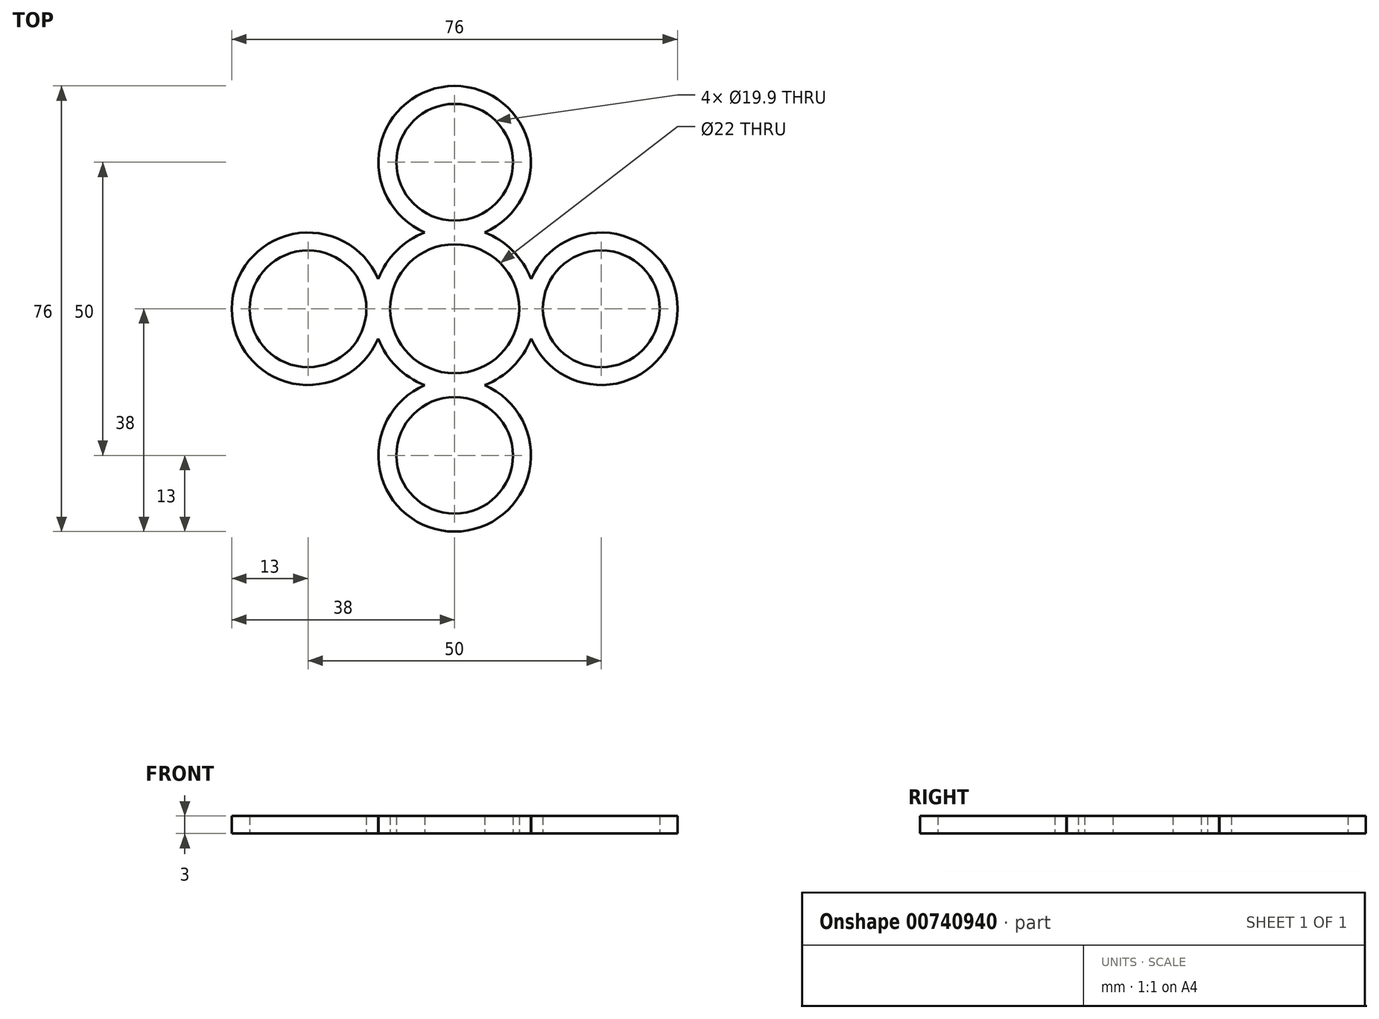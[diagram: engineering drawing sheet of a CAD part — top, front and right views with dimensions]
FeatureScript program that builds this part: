
annotation { "Feature Type Name" : "Feature", "Feature Type Description" : "" }
export const myFeature = defineFeature(function(context is Context, id is Id, definition is map)
    precondition{}
    {
        {
            var Q0;
            Q0=qCreatedBy(makeId("Top.planeOp"),FACE);
            var sketch = newSketch(context, id + "F0", { "sketchPlane" : qUnion([Q0])});
            skArc(sketch, "E0", {"start": v(7.78, 7.78) * mm, "mid": v(0, 11) * mm, "end": v(-7.78, 7.78) * mm});
            skCircle(sketch, "E1", {"center": v(0, 25) * mm, "radius": 9.95 * mm});
            skArc(sketch, "E2", {"start": v(-5.1, 13.04) * mm, "mid": v(-7.66, 11.72) * mm, "end": v(-9.9, 9.9) * mm});
            skArc(sketch, "E3", {"start": v(5.1, 13.04) * mm, "mid": v(0, 38) * mm, "end": v(-5.1, 13.04) * mm});
            skArc(sketch, "E4.trimOffspring", {"start": v(9.9, 9.9) * mm, "mid": v(7.66, 11.72) * mm, "end": v(5.1, 13.04) * mm});
            skArc(sketch, "E5.1.0", {"start": v(-13.04, 5.1) * mm, "mid": v(-38, 0) * mm, "end": v(-13.04, -5.1) * mm});
            skCircle(sketch, "E5.1.1", {"center": v(-25, 0) * mm, "radius": 9.95 * mm});
            skArc(sketch, "E5.1.2", {"start": v(-7.78, 7.78) * mm, "mid": v(-11, 0) * mm, "end": v(-7.78, -7.78) * mm});
            skArc(sketch, "E5.1.3", {"start": v(-13.04, -5.1) * mm, "mid": v(-11.72, -7.66) * mm, "end": v(-9.9, -9.9) * mm});
            skArc(sketch, "E5.1.4", {"start": v(-9.9, 9.9) * mm, "mid": v(-11.72, 7.66) * mm, "end": v(-13.04, 5.1) * mm});
            skArc(sketch, "E5.2.0", {"start": v(-5.1, -13.04) * mm, "mid": v(0, -38) * mm, "end": v(5.1, -13.04) * mm});
            skCircle(sketch, "E5.2.1", {"center": v(0, -25) * mm, "radius": 9.95 * mm});
            skArc(sketch, "E5.2.2", {"start": v(-7.78, -7.78) * mm, "mid": v(0, -11) * mm, "end": v(7.78, -7.78) * mm});
            skArc(sketch, "E5.2.3", {"start": v(5.1, -13.04) * mm, "mid": v(7.66, -11.72) * mm, "end": v(9.9, -9.9) * mm});
            skArc(sketch, "E5.2.4", {"start": v(-9.9, -9.9) * mm, "mid": v(-7.66, -11.72) * mm, "end": v(-5.1, -13.04) * mm});
            skArc(sketch, "E5.3.0", {"start": v(13.04, -5.1) * mm, "mid": v(38, 0) * mm, "end": v(13.04, 5.1) * mm});
            skCircle(sketch, "E5.3.1", {"center": v(25, 0) * mm, "radius": 9.95 * mm});
            skArc(sketch, "E5.3.2", {"start": v(7.78, -7.78) * mm, "mid": v(11, 0) * mm, "end": v(7.78, 7.78) * mm});
            skArc(sketch, "E5.3.3", {"start": v(13.04, 5.1) * mm, "mid": v(11.72, 7.66) * mm, "end": v(9.9, 9.9) * mm});
            skArc(sketch, "E5.3.4", {"start": v(9.9, -9.9) * mm, "mid": v(11.72, -7.66) * mm, "end": v(13.04, -5.1) * mm});
            skSolve(sketch);
        }
        {
            var Q0;
            Q0 = qSketchRegion(id + "F0", true);
            extrude(context, id + "F1", {"entities" : qUnion([Q0]), "depth" : 3 * mm, "offsetDistance" : 25 * mm});
        }
    });
